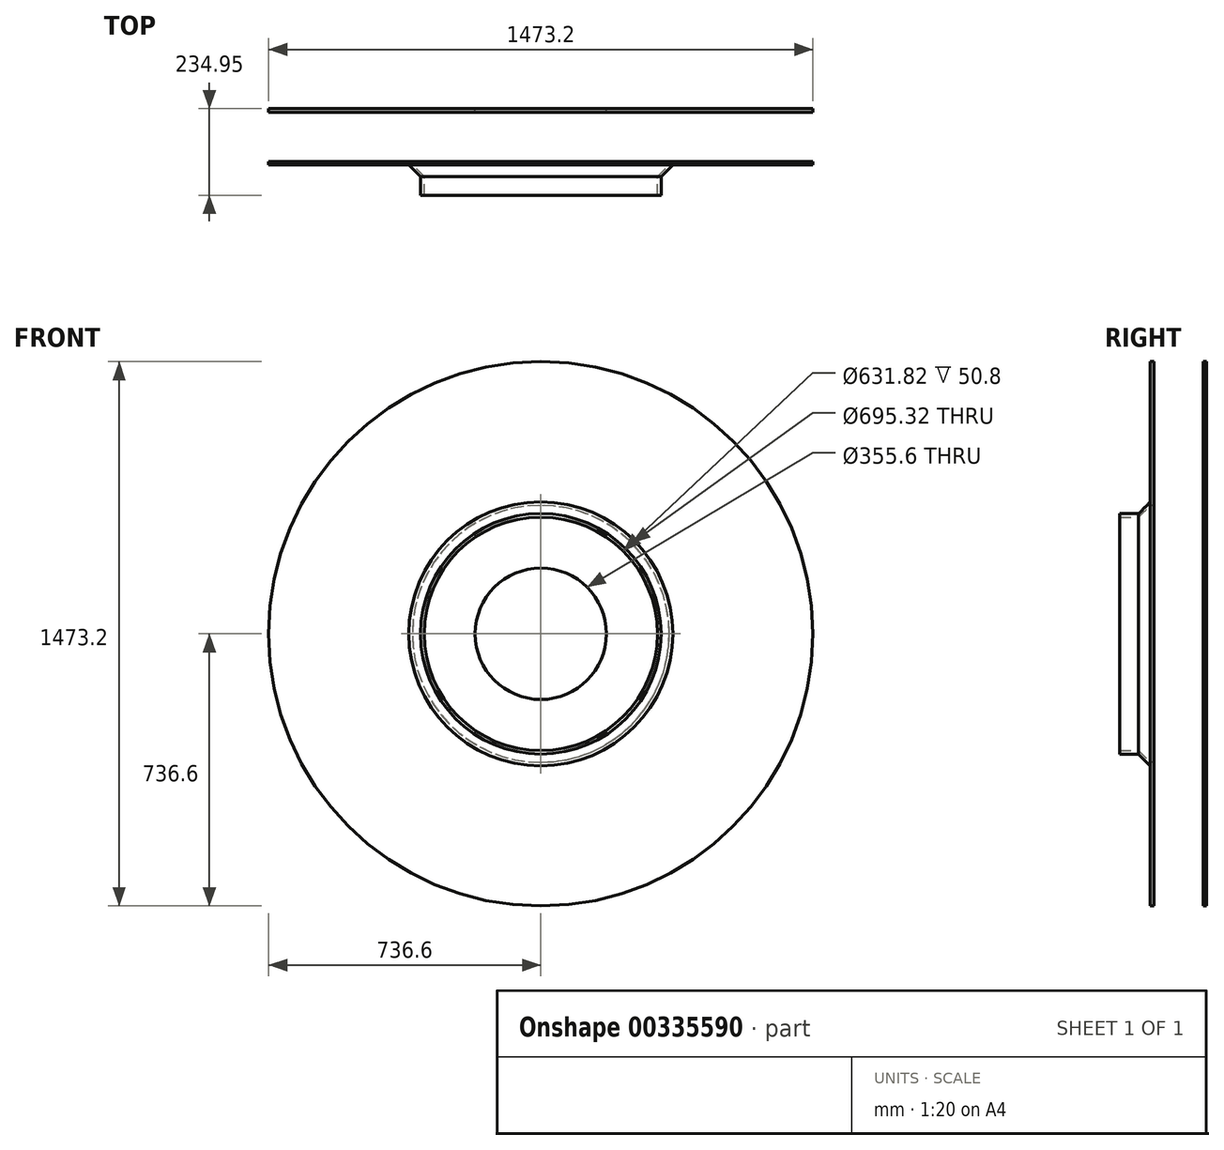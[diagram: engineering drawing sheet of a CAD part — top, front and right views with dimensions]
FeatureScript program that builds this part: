
annotation { "Feature Type Name" : "Feature", "Feature Type Description" : "" }
export const myFeature = defineFeature(function(context is Context, id is Id, definition is map)
    precondition{}
    {
        {
            var Q0;
            Q0=qCreatedBy(makeId("Front.planeOp"),FACE);
            var sketch = newSketch(context, id + "F0", { "sketchPlane" : qUnion([Q0])});
            skCircle(sketch, "E0", {"center": v(0, 0) * mm, "radius": 736.6 * mm});
            skSolve(sketch);
        }
        {
            var Q0;
            Q0=makeQuery(id+"F0.imprint","IMPRINT",FACE,{"disambiguationData":[TD([[makeQuery(id+"F0.imprint","IMPRINT",EDGE,{"derivedFrom":sQuery(id+"F0.wireOp",EDGE,"E0")}),1.0]])]});
            extrude(context, id + "F1", {"entities" : qUnion([Q0]), "depth" : 9.52 * mm});
        }
        {
            var Q0;
            Q0=makeQuery(id+"F1.opExtrude","CAP_FACE",FACE,{"disambiguationData":[OSD([sQuery(id+"F0.wireOp",EDGE,"E0")])],"isStart":false});
            cPlane(context, id + "F2", {"entities" : qUnion([Q0]), "cplaneType" : CPlaneType.OFFSET, "offset" : 133.35 * mm, "width" : 152.4 * mm, "height" : 152.4 * mm});
        }
        {
            var Q0;
            Q0=qCreatedBy(id+"F2.planeOp",FACE);
            var sketch = newSketch(context, id + "F3", { "sketchPlane" : qUnion([Q0])});
            skCircle(sketch, "E1", {"center": v(0, 0) * mm, "radius": 736.6 * mm});
            skSolve(sketch);
        }
        {
            var Q0;
            Q0 = qSketchRegion(id + "F3", true);
            extrude(context, id + "F4", {"entities" : qUnion([Q0]), "depth" : 9.52 * mm});
        }
        {
            var Q0;
            Q0=makeQuery(id+"F4.opExtrude","CAP_FACE",FACE,{"disambiguationData":[OSD([sQuery(id+"F3.wireOp",EDGE,"E1")])],"isStart":false});
            cPlane(context, id + "F5", {"entities" : qUnion([Q0]), "cplaneType" : CPlaneType.OFFSET, "offset" : 31.75 * mm, "width" : 152.4 * mm, "height" : 152.4 * mm});
        }
        {
            var Q0;
            Q0=qCreatedBy(id+"F5.planeOp",FACE);
            var sketch = newSketch(context, id + "F6", { "sketchPlane" : qUnion([Q0])});
            skCircle(sketch, "E2", {"center": v(0, 0) * mm, "radius": 325.44 * mm});
            skCircle(sketch, "E3", {"center": v(0, 0) * mm, "radius": 315.91 * mm});
            skSolve(sketch);
        }
        {
            var Q0;
            Q0=makeQuery(id+"F4.opExtrude","CAP_FACE",FACE,{"disambiguationData":[OSD([sQuery(id+"F3.wireOp",EDGE,"E1")])],"isStart":false});
            var sketch = newSketch(context, id + "F7", { "sketchPlane" : qUnion([Q0])});
            skCircle(sketch, "E4", {"center": v(0, 0) * mm, "radius": 357.19 * mm});
            skCircle(sketch, "E5", {"center": v(0, 0) * mm, "radius": 347.66 * mm});
            skSolve(sketch);
        }
        {
            var Q0;
            Q0=qCreatedBy(makeId("Right.planeOp"),FACE);
            var sketch = newSketch(context, id + "F8", { "sketchPlane" : qUnion([Q0])});
            skLineSegment(sketch, "E6", {"start": v(-184.15, 315.91) * mm, "end": v(-152.4, 347.66) * mm});
            skLineSegment(sketch, "E7", {"start": v(-152.4, 357.19) * mm, "end": v(-184.15, 325.44) * mm});
            skLineSegment(sketch, "E8", {"start": v(-184.15, 325.44) * mm, "end": v(-184.15, 315.91) * mm});
            skLineSegment(sketch, "E9", {"start": v(-152.4, 347.66) * mm, "end": v(-152.4, 357.19) * mm});
            skLineSegment(sketch, "E10", {"start": v(-184.15, 325.44) * mm, "end": v(-234.95, 325.44) * mm});
            skLineSegment(sketch, "E11", {"start": v(-234.95, 325.44) * mm, "end": v(-234.95, 315.91) * mm});
            skLineSegment(sketch, "E12", {"start": v(-234.95, 315.91) * mm, "end": v(-184.15, 315.91) * mm});
            skSolve(sketch);
        }
        {
            var Q0;
            Q0=makeQuery(id+"F8.imprint","IMPRINT",FACE,{"disambiguationData":[TD([[makeQuery(id+"F8.imprint","IMPRINT",EDGE,{"derivedFrom":sQuery(id+"F8.wireOp",EDGE,"E6")}),1.0]])]});
            var Q1;
            Q1=makeQuery(id+"F8.imprint","IMPRINT",FACE,{"disambiguationData":[TD([[makeQuery(id+"F8.imprint","IMPRINT",EDGE,{"derivedFrom":sQuery(id+"F8.wireOp",EDGE,"E8")}),-1.0]])]});
            var Q2;
            Q2=makeQuery(id+"F4.opExtrude","CAP_EDGE",EDGE,{"disambiguationData":[OSD([sQuery(id+"F3.wireOp",EDGE,"E1")])],"isStart":false});
            revolve(context, id + "F9", {"operationType" : NewBodyOperationType.ADD, "entities" : qUnion([Q0, Q1]), "axis" : qUnion([Q2]), "revolveType" : RevolveType.FULL});
        }
        {
            var Q0;
            Q0=makeQuery(id+"F7.imprint","IMPRINT",FACE,{"disambiguationData":[TD([[makeQuery(id+"F7.imprint","IMPRINT",EDGE,{"derivedFrom":sQuery(id+"F7.wireOp",EDGE,"E5")}),1.0]])]});
            var Q1;
            Q1=sQuery(id+"F7.wireOp",EDGE,"E5");
            extrude(context, id + "F10", {"entities" : qUnion([Q0]), "operationType" : NewBodyOperationType.REMOVE, "surfaceEntities" : qUnion([Q1]), "oppositeDirection" : true, "depth" : 25.4 * mm});
        }
        {
            var Q0;
            Q0=makeQuery(id+"F1.opExtrude","CAP_FACE",FACE,{"disambiguationData":[OSD([sQuery(id+"F0.wireOp",EDGE,"E0")])],"isStart":true});
            var sketch = newSketch(context, id + "F11", { "sketchPlane" : qUnion([Q0])});
            skCircle(sketch, "E13", {"center": v(0, 0) * mm, "radius": 177.8 * mm});
            skSolve(sketch);
        }
        {
            var Q0;
            Q0 = qSketchRegion(id + "F11", true);
            extrude(context, id + "F12", {"entities" : qUnion([Q0]), "operationType" : NewBodyOperationType.REMOVE, "oppositeDirection" : true, "depth" : 25.4 * mm});
        }
    });
